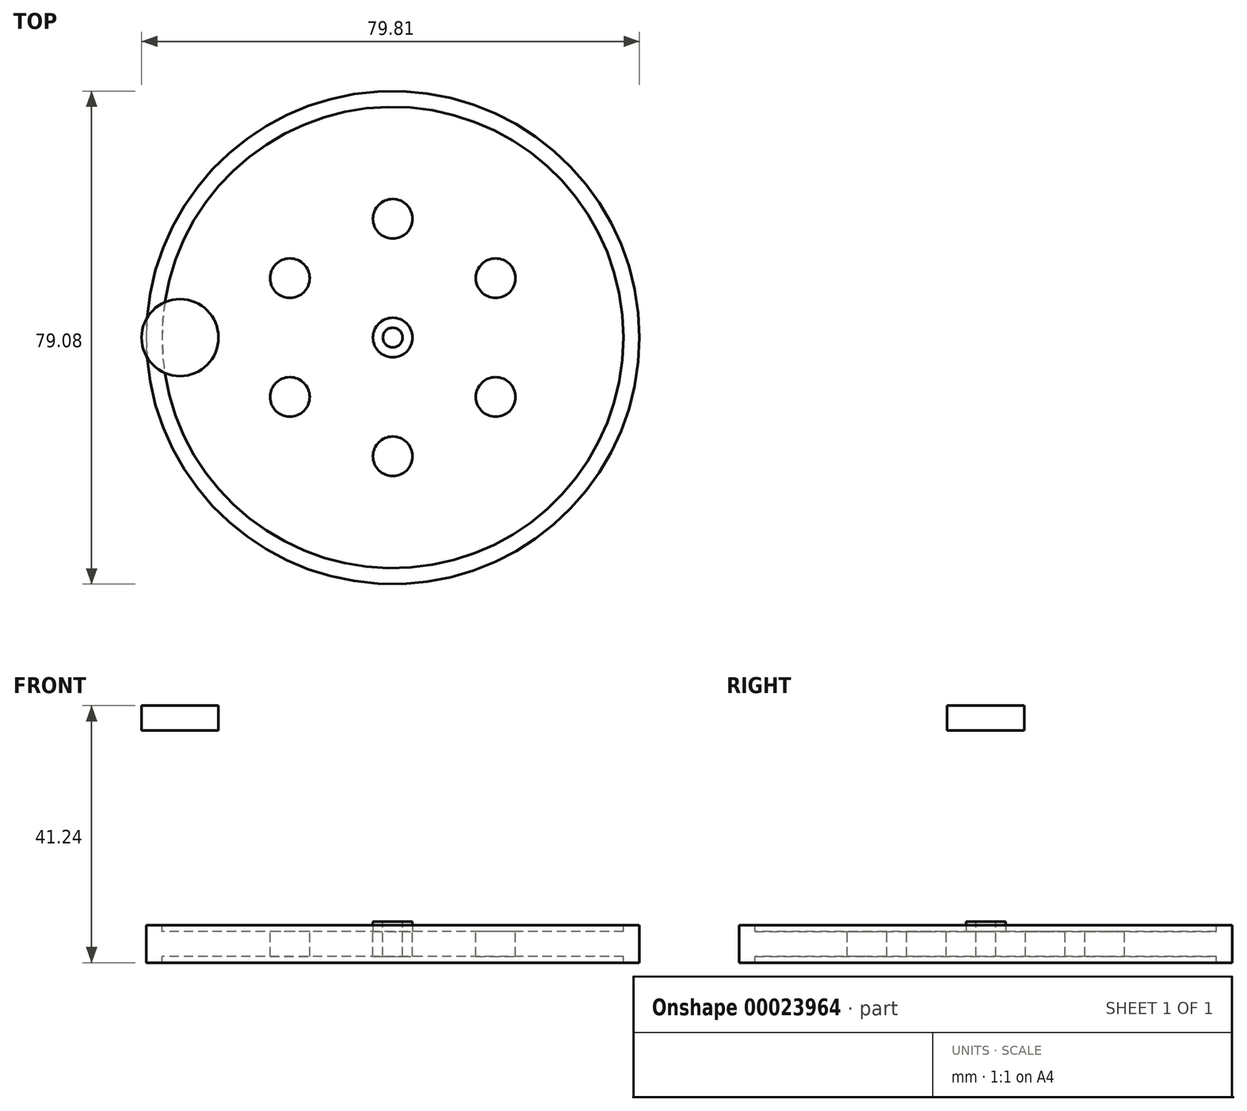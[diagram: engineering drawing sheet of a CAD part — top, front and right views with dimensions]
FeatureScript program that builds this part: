
annotation { "Feature Type Name" : "Feature", "Feature Type Description" : "" }
export const myFeature = defineFeature(function(context is Context, id is Id, definition is map)
    precondition{}
    {
        {
            var Q0;
            Q0=qCreatedBy(makeId("Front.planeOp"),FACE);
            var sketch = newSketch(context, id + "F0", { "sketchPlane" : qUnion([Q0])});
            skLineSegment(sketch, "E0.bottom", {"start": v(-34.5, 0.81) * mm, "end": v(1.22, 0.81) * mm});
            skLineSegment(sketch, "E0.top", {"start": v(-34.5, -3.19) * mm, "end": v(1.22, -3.19) * mm});
            skLineSegment(sketch, "E0.left", {"start": v(-34.5, 0.81) * mm, "end": v(-34.5, -3.19) * mm});
            skLineSegment(sketch, "E0.right", {"start": v(1.22, 0.81) * mm, "end": v(1.22, -3.19) * mm});
            skLineSegment(sketch, "E1.bottom", {"start": v(-34.5, -4.19) * mm, "end": v(-37.05, -4.19) * mm});
            skLineSegment(sketch, "E1.top", {"start": v(-34.5, 1.81) * mm, "end": v(-37.05, 1.81) * mm});
            skLineSegment(sketch, "E1.left", {"start": v(-34.5, -4.19) * mm, "end": v(-34.5, 1.81) * mm});
            skLineSegment(sketch, "E1.right", {"start": v(-37.05, -4.19) * mm, "end": v(-37.05, 1.81) * mm});
            skLineSegment(sketch, "E2", {"start": v(2.5, 1.81) * mm, "end": v(2.5, -11.14) * mm, "construction": true});
            skPoint(sketch, "E3.bottom.start.orphan", {"position": v(1.22, 1.81) * mm});
            skSolve(sketch);
        }
        {
            var Q0;
            Q0 = qSketchRegion(id + "F0", true);
            var Q1;
            Q1=sQuery(id+"F0.wireOp",EDGE,"E2");
            revolve(context, id + "F1", {"entities" : qUnion([Q0]), "axis" : qUnion([Q1]), "revolveType" : RevolveType.FULL});
        }
        {
            var Q0;
            Q0=makeQuery(id+"F1.opRevolve","SWEPT_FACE",FACE,{"disambiguationData":[OSD([sQuery(id+"F0.wireOp",EDGE,"E0.bottom")])]});
            var sketch = newSketch(context, id + "F2", { "sketchPlane" : qUnion([Q0])});
            skCircle(sketch, "E4", {"center": v(2.5, 0) * mm, "radius": 1.59 * mm});
            skLineSegment(sketch, "E5", {"start": v(2.5, 0) * mm, "end": v(2.5, 37) * mm});
            skCircle(sketch, "E6", {"center": v(2.5, 19.05) * mm, "radius": 3.18 * mm});
            skCircle(sketch, "E7.1.0", {"center": v(-14, 9.53) * mm, "radius": 3.18 * mm});
            skCircle(sketch, "E7.2.0", {"center": v(-14, -9.52) * mm, "radius": 3.18 * mm});
            skCircle(sketch, "E7.3.0", {"center": v(2.5, -19.05) * mm, "radius": 3.18 * mm});
            skCircle(sketch, "E7.4.0", {"center": v(19, -9.53) * mm, "radius": 3.18 * mm});
            skCircle(sketch, "E7.5.0", {"center": v(19, 9.53) * mm, "radius": 3.18 * mm});
            skSolve(sketch);
        }
        {
            var Q0;
            Q0=makeQuery(id+"F2.imprint","IMPRINT",FACE,{"disambiguationData":[TD([[makeQuery(id+"F2.imprint","IMPRINT",EDGE,{"derivedFrom":sQuery(id+"F2.wireOp",EDGE,"E7.1.0")}),1.0]])]});
            var Q1;
            Q1=makeQuery(id+"F2.imprint","IMPRINT",FACE,{"disambiguationData":[TD([[makeQuery(id+"F2.imprint","IMPRINT",EDGE,{"derivedFrom":sQuery(id+"F2.wireOp",EDGE,"E7.2.0")}),1.0]])]});
            var Q2;
            Q2=makeQuery(id+"F2.imprint","IMPRINT",FACE,{"disambiguationData":[TD([[makeQuery(id+"F2.imprint","IMPRINT",EDGE,{"derivedFrom":sQuery(id+"F2.wireOp",EDGE,"E7.3.0")}),1.0]])]});
            var Q3;
            Q3=makeQuery(id+"F2.imprint","IMPRINT",FACE,{"disambiguationData":[TD([[makeQuery(id+"F2.imprint","IMPRINT",EDGE,{"derivedFrom":sQuery(id+"F2.wireOp",EDGE,"E7.4.0")}),1.0]])]});
            var Q4;
            Q4=makeQuery(id+"F2.imprint","IMPRINT",FACE,{"disambiguationData":[TD([[makeQuery(id+"F2.imprint","IMPRINT",EDGE,{"derivedFrom":sQuery(id+"F2.wireOp",EDGE,"E7.5.0")}),1.0]])]});
            var Q5;
            Q5=makeQuery(id+"F2.imprint","IMPRINT",FACE,{"disambiguationData":[TD([[makeQuery(id+"F2.imprint","IMPRINT",EDGE,{"derivedFrom":makeQuery(id+"F1.opRevolve","SWEPT_EDGE",EDGE,{"disambiguationData":[OSD([sQuery(id+"F0.wireOp",EDGE,"E0.bottom"),sQuery(id+"F0.wireOp",EDGE,"E0.right")])]})}),1.0]])]});
            var Q6;
            {var subQ0=sQuery(id+"F2.wireOp",EDGE,"E6");var subQ1=sQuery(id+"F2.wireOp",EDGE,"E5");var subQ3=makeQuery(id+"F2.imprint","INTERSECT",VERTEX,{"disambiguationData":[OD(0.0)],"derivedFrom":[subQ1,subQ0]});Q6=makeQuery(id+"F2.imprint","IMPRINT",FACE,{"disambiguationData":[TD([[makeQuery(id+"F2.imprint","IMPRINT",EDGE,{"disambiguationData":[TD([[subQ3,-1.0]])],"derivedFrom":subQ1}),1.0]])]});}
            var Q7;
            {var subQ0=sQuery(id+"F2.wireOp",EDGE,"E6");var subQ1=sQuery(id+"F2.wireOp",EDGE,"E5");var subQ3=makeQuery(id+"F2.imprint","INTERSECT",VERTEX,{"disambiguationData":[OD(0.0)],"derivedFrom":[subQ1,subQ0]});Q7=makeQuery(id+"F2.imprint","IMPRINT",FACE,{"disambiguationData":[TD([[makeQuery(id+"F2.imprint","IMPRINT",EDGE,{"disambiguationData":[TD([[subQ3,-1.0]])],"derivedFrom":subQ1}),-1.0]])]});}
            var Q8;
            Q8=makeQuery(id+"F1.opRevolve","SWEPT_FACE",FACE,{"disambiguationData":[OSD([sQuery(id+"F0.wireOp",EDGE,"E3.bottom")])]});
            var Q9;
            Q9=makeQuery(id+"F2.imprint","IMPRINT",FACE,{"disambiguationData":[TD([[makeQuery(id+"F2.imprint","IMPRINT",EDGE,{"derivedFrom":sQuery(id+"F2.wireOp",EDGE,"E4")}),1.0]])]});
            extrude(context, id + "F3", {"entities" : qUnion([Q0, Q1, Q2, Q3, Q4, Q5, Q6, Q7, Q8, Q9]), "operationType" : NewBodyOperationType.REMOVE, "endBound" : BoundingType.THROUGH_ALL, "oppositeDirection" : true, "depth" : 25.4 * mm});
        }
        {
            var Q0;
            Q0=qCreatedBy(makeId("Front.planeOp"),FACE);
            var sketch = newSketch(context, id + "F4", { "sketchPlane" : qUnion([Q0])});
            skLineSegment(sketch, "E8", {"start": v(-31.61, 33.05) * mm, "end": v(-31.61, 42.44) * mm, "construction": true});
            skLineSegment(sketch, "E9.left", {"start": v(-37.78, 37.05) * mm, "end": v(-37.78, 33.05) * mm});
            skLineSegment(sketch, "E9.bottom", {"start": v(-37.78, 37.05) * mm, "end": v(-32.4, 37.05) * mm});
            skLineSegment(sketch, "E9.top", {"start": v(-37.78, 33.05) * mm, "end": v(-32.4, 33.05) * mm});
            skLineSegment(sketch, "E10.right", {"start": v(-31.61, 37.05) * mm, "end": v(-31.61, 33.05) * mm});
            skLineSegment(sketch, "E10.top", {"start": v(-32.4, 33.05) * mm, "end": v(-31.61, 33.05) * mm});
            skLineSegment(sketch, "E10.bottom", {"start": v(-32.4, 37.05) * mm, "end": v(-31.61, 37.05) * mm});
            skSolve(sketch);
        }
        {
            var Q0;
            Q0=makeQuery(id+"F4.imprint","IMPRINT",FACE,{"disambiguationData":[TD([[makeQuery(id+"F4.imprint","IMPRINT",EDGE,{"derivedFrom":sQuery(id+"F4.wireOp",EDGE,"E9.left")}),1.0]])]});
            var Q1;
            Q1 = qConstructionFilter(qBodyType(qCreatedBy(id + "F4" ,EDGE), BodyType.WIRE), ConstructionObject.NO);
            var Q2;
            Q2=sQuery(id+"F4.wireOp",EDGE,"E8");
            revolve(context, id + "F5", {"entities" : qUnion([Q0]), "surfaceEntities" : qUnion([Q1]), "axis" : qUnion([Q2]), "revolveType" : RevolveType.FULL});
        }
        {
            var Q0;
            Q0=makeQuery(id+"F1.opRevolve","SWEPT_FACE",FACE,{"disambiguationData":[OSD([sQuery(id+"F0.wireOp",EDGE,"E0.bottom")])]});
            var sketch = newSketch(context, id + "F6", { "sketchPlane" : qUnion([Q0])});
            skCircle(sketch, "E11", {"center": v(2.5, 0) * mm, "radius": 3.18 * mm});
            skCircle(sketch, "E12", {"center": v(2.5, 0) * mm, "radius": 1.59 * mm});
            skSolve(sketch);
        }
        {
            var Q0;
            Q0 = qSketchRegion(id + "F6", true);
            extrude(context, id + "F7", {"entities" : qUnion([Q0]), "operationType" : NewBodyOperationType.ADD, "depth" : 1.59 * mm});
        }
    });
